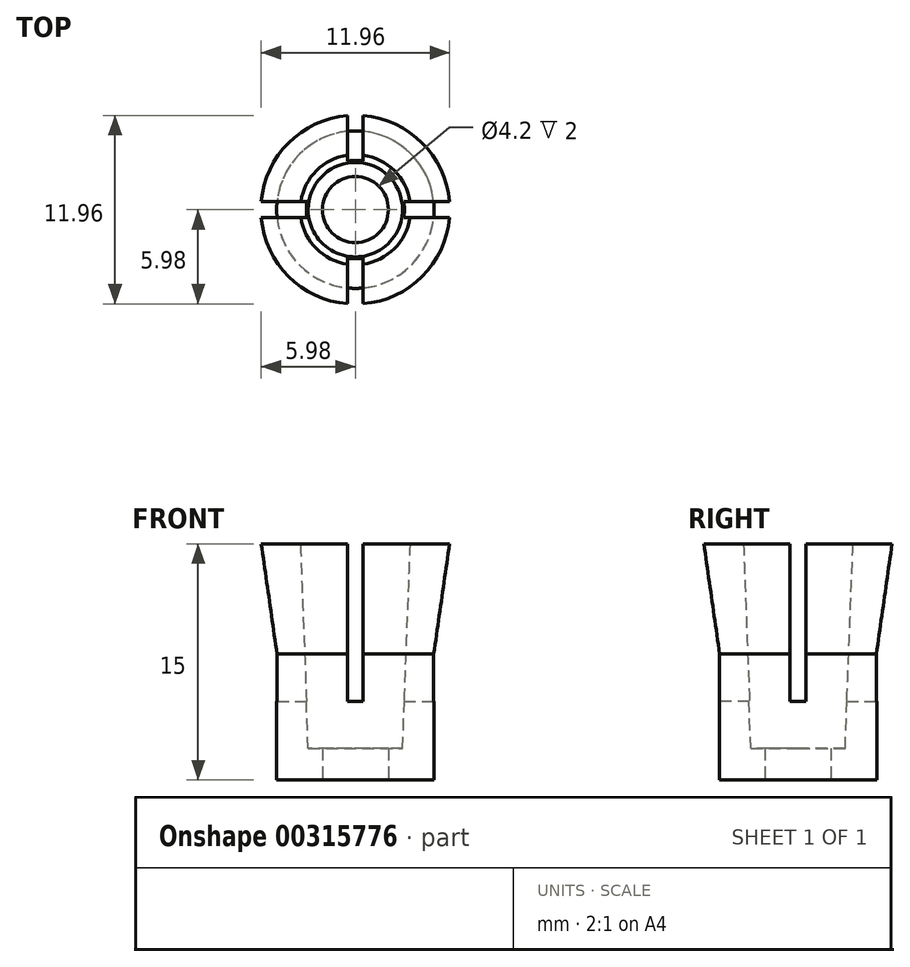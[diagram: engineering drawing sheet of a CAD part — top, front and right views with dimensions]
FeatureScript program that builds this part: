
annotation { "Feature Type Name" : "Feature", "Feature Type Description" : "" }
export const myFeature = defineFeature(function(context is Context, id is Id, definition is map)
    precondition{}
    {
        {
            var Q0;
            Q0=qCreatedBy(makeId("Front.planeOp"),FACE);
            var sketch = newSketch(context, id + "F0", { "sketchPlane" : qUnion([Q0])});
            skLineSegment(sketch, "E0", {"start": v(0, 0) * mm, "end": v(0, 2) * mm});
            skLineSegment(sketch, "E1", {"start": v(0, 0) * mm, "end": v(-5, 0) * mm});
            skLineSegment(sketch, "E2", {"start": v(-5, 0) * mm, "end": v(-5, 8) * mm});
            skLineSegment(sketch, "E3", {"start": v(-5, 8) * mm, "end": v(-6, 15) * mm});
            skLineSegment(sketch, "E4", {"start": v(-6, 15) * mm, "end": v(-3.5, 15) * mm});
            skLineSegment(sketch, "E5", {"start": v(-3.5, 15) * mm, "end": v(-3, 2) * mm});
            skLineSegment(sketch, "E6", {"start": v(-3, 2) * mm, "end": v(0, 2) * mm});
            skSolve(sketch);
        }
        {
            var Q0;
            Q0=makeQuery(id+"F0.imprint","IMPRINT",FACE,{"disambiguationData":[TD([[makeQuery(id+"F0.imprint","IMPRINT",EDGE,{"derivedFrom":sQuery(id+"F0.wireOp",EDGE,"E0")}),1.0]])]});
            var Q1;
            Q1=sQuery(id+"F0.wireOp",EDGE,"E2");
            var Q2;
            Q2=sQuery(id+"F0.wireOp",EDGE,"E3");
            var Q3;
            Q3=sQuery(id+"F0.wireOp",EDGE,"E4");
            var Q4;
            Q4=sQuery(id+"F0.wireOp",EDGE,"E0");
            var Q5;
            Q5=sQuery(id+"F0.wireOp",EDGE,"E1");
            var Q6;
            Q6=sQuery(id+"F0.wireOp",EDGE,"E0");
            revolve(context, id + "F1", {"entities" : qUnion([Q0]), "surfaceEntities" : qUnion([Q1, Q2, Q3, Q4, Q5]), "axis" : qUnion([Q6]), "revolveType" : RevolveType.FULL});
        }
        {
            var Q0;
            Q0=makeQuery(id+"F1.opRevolve","SWEPT_FACE",FACE,{"disambiguationData":[OSD([sQuery(id+"F0.wireOp",EDGE,"E1")])]});
            var sketch = newSketch(context, id + "F2", { "sketchPlane" : qUnion([Q0])});
            skPoint(sketch, "E7", {"position": v(0, 0) * mm});
            skSolve(sketch);
        }
        {
            var Q0;
            Q0=sQuery(id+"F2.wireOp",VERTEX,"E7");
            var Q1;
            Q1=makeQuery(id+"F1.opRevolve","SWEPT_BODY",BODY,{"disambiguationData":[OSD([sQuery(id+"F0.wireOp",EDGE,"E0"),sQuery(id+"F0.wireOp",EDGE,"E1"),sQuery(id+"F0.wireOp",EDGE,"E2"),sQuery(id+"F0.wireOp",EDGE,"E3"),sQuery(id+"F0.wireOp",EDGE,"E4"),sQuery(id+"F0.wireOp",EDGE,"E5"),sQuery(id+"F0.wireOp",EDGE,"E6")])]});
            hole(context, id + "F3", {"style" : HoleStyle.SIMPLE, "endStyle" : HoleEndStyle.THROUGH, "standardTappedOrClearance" : lookupTablePath({ "standard" : "ISO", "engagement" : "75%", "pitch" : "0.8 mm", "size" : "M5", "type" : "Tapped" }), "standardBlindInLast" : lookupTablePath({ "standard" : "ISO", "engagement" : "75%", "pitch" : "0.8 mm", "size" : "M5", "type" : "Tapped" }), "holeDiameter" : 4.2 * mm, "showTappedDepth" : true, "tappedDepth" : 12 * mm, "tapClearance" : 3, "locations" : qUnion([Q0]), "scope" : qUnion([Q1]), "majorDiameter" : 5 * mm});
        }
        {
            var Q0;
            Q0=makeQuery(id+"F1.opRevolve","SWEPT_FACE",FACE,{"disambiguationData":[OSD([sQuery(id+"F0.wireOp",EDGE,"E4")])]});
            var sketch = newSketch(context, id + "F4", { "sketchPlane" : qUnion([Q0])});
            skArc(sketch, "E8.0", {"start": v(-0.5, 5.98) * mm, "mid": v(0, 6) * mm, "end": v(0.5, 5.98) * mm});
            skArc(sketch, "E9.0", {"start": v(0.5, 2.04) * mm, "mid": v(0, 2.1) * mm, "end": v(-0.5, 2.04) * mm});
            skLineSegment(sketch, "E10", {"start": v(0.5, 2.04) * mm, "end": v(0.5, 5.98) * mm});
            skLineSegment(sketch, "E11", {"start": v(-0.5, 5.98) * mm, "end": v(-0.5, 2.04) * mm});
            skLineSegment(sketch, "E12", {"start": v(0, 0) * mm, "end": v(0, 6) * mm, "construction": true});
            skLineSegment(sketch, "E13.1.0", {"start": v(-2.04, 0.5) * mm, "end": v(-5.98, 0.5) * mm});
            skArc(sketch, "E13.1.1", {"start": v(-5.98, -0.5) * mm, "mid": v(-6, 0) * mm, "end": v(-5.98, 0.5) * mm});
            skArc(sketch, "E13.1.2", {"start": v(-2.04, 0.5) * mm, "mid": v(-2.1, 0) * mm, "end": v(-2.04, -0.5) * mm});
            skLineSegment(sketch, "E13.1.3", {"start": v(-5.98, -0.5) * mm, "end": v(-2.04, -0.5) * mm});
            skLineSegment(sketch, "E13.2.0", {"start": v(-0.5, -2.04) * mm, "end": v(-0.5, -5.98) * mm});
            skArc(sketch, "E13.2.1", {"start": v(0.5, -5.98) * mm, "mid": v(0, -6) * mm, "end": v(-0.5, -5.98) * mm});
            skArc(sketch, "E13.2.2", {"start": v(-0.5, -2.04) * mm, "mid": v(0, -2.1) * mm, "end": v(0.5, -2.04) * mm});
            skLineSegment(sketch, "E13.2.3", {"start": v(0.5, -5.98) * mm, "end": v(0.5, -2.04) * mm});
            skLineSegment(sketch, "E13.3.0", {"start": v(2.04, -0.5) * mm, "end": v(5.98, -0.5) * mm});
            skArc(sketch, "E13.3.1", {"start": v(5.98, 0.5) * mm, "mid": v(6, 0) * mm, "end": v(5.98, -0.5) * mm});
            skArc(sketch, "E13.3.2", {"start": v(2.04, -0.5) * mm, "mid": v(2.1, 0) * mm, "end": v(2.04, 0.5) * mm});
            skLineSegment(sketch, "E13.3.3", {"start": v(5.98, 0.5) * mm, "end": v(2.04, 0.5) * mm});
            skSolve(sketch);
        }
        {
            var Q0;
            {var subQ0=sQuery(id+"F4.wireOp",EDGE,"E13.1.2");Q0=makeQuery(id+"F4.imprint","IMPRINT",FACE,{"disambiguationData":[TD([[makeQuery(id+"F4.imprint","IMPRINT",EDGE,{"derivedFrom":subQ0}),-1.0]])]});}
            var Q1;
            {var subQ0=sQuery(id+"F4.wireOp",EDGE,"E13.1.1");Q1=makeQuery(id+"F4.imprint","IMPRINT",FACE,{"disambiguationData":[TD([[makeQuery(id+"F4.imprint","IMPRINT",EDGE,{"derivedFrom":subQ0}),-1.0]])]});}
            var Q2;
            {var subQ0=sQuery(id+"F4.wireOp",EDGE,"E9.0");Q2=makeQuery(id+"F4.imprint","IMPRINT",FACE,{"disambiguationData":[TD([[makeQuery(id+"F4.imprint","IMPRINT",EDGE,{"derivedFrom":subQ0}),-1.0]])]});}
            var Q3;
            {var subQ0=sQuery(id+"F4.wireOp",EDGE,"E8.0");Q3=makeQuery(id+"F4.imprint","IMPRINT",FACE,{"disambiguationData":[TD([[makeQuery(id+"F4.imprint","IMPRINT",EDGE,{"derivedFrom":subQ0}),-1.0]])]});}
            var Q4;
            {var subQ0=sQuery(id+"F4.wireOp",EDGE,"E13.3.2");Q4=makeQuery(id+"F4.imprint","IMPRINT",FACE,{"disambiguationData":[TD([[makeQuery(id+"F4.imprint","IMPRINT",EDGE,{"derivedFrom":subQ0}),-1.0]])]});}
            var Q5;
            {var subQ0=sQuery(id+"F4.wireOp",EDGE,"E13.3.1");Q5=makeQuery(id+"F4.imprint","IMPRINT",FACE,{"disambiguationData":[TD([[makeQuery(id+"F4.imprint","IMPRINT",EDGE,{"derivedFrom":subQ0}),-1.0]])]});}
            var Q6;
            {var subQ0=sQuery(id+"F4.wireOp",EDGE,"E13.2.2");Q6=makeQuery(id+"F4.imprint","IMPRINT",FACE,{"disambiguationData":[TD([[makeQuery(id+"F4.imprint","IMPRINT",EDGE,{"derivedFrom":subQ0}),-1.0]])]});}
            var Q7;
            {var subQ0=sQuery(id+"F4.wireOp",EDGE,"E13.2.1");Q7=makeQuery(id+"F4.imprint","IMPRINT",FACE,{"disambiguationData":[TD([[makeQuery(id+"F4.imprint","IMPRINT",EDGE,{"derivedFrom":subQ0}),-1.0]])]});}
            extrude(context, id + "F5", {"entities" : qUnion([Q0, Q1, Q2, Q3, Q4, Q5, Q6, Q7]), "operationType" : NewBodyOperationType.REMOVE, "oppositeDirection" : true, "depth" : 10 * mm});
        }
    });
